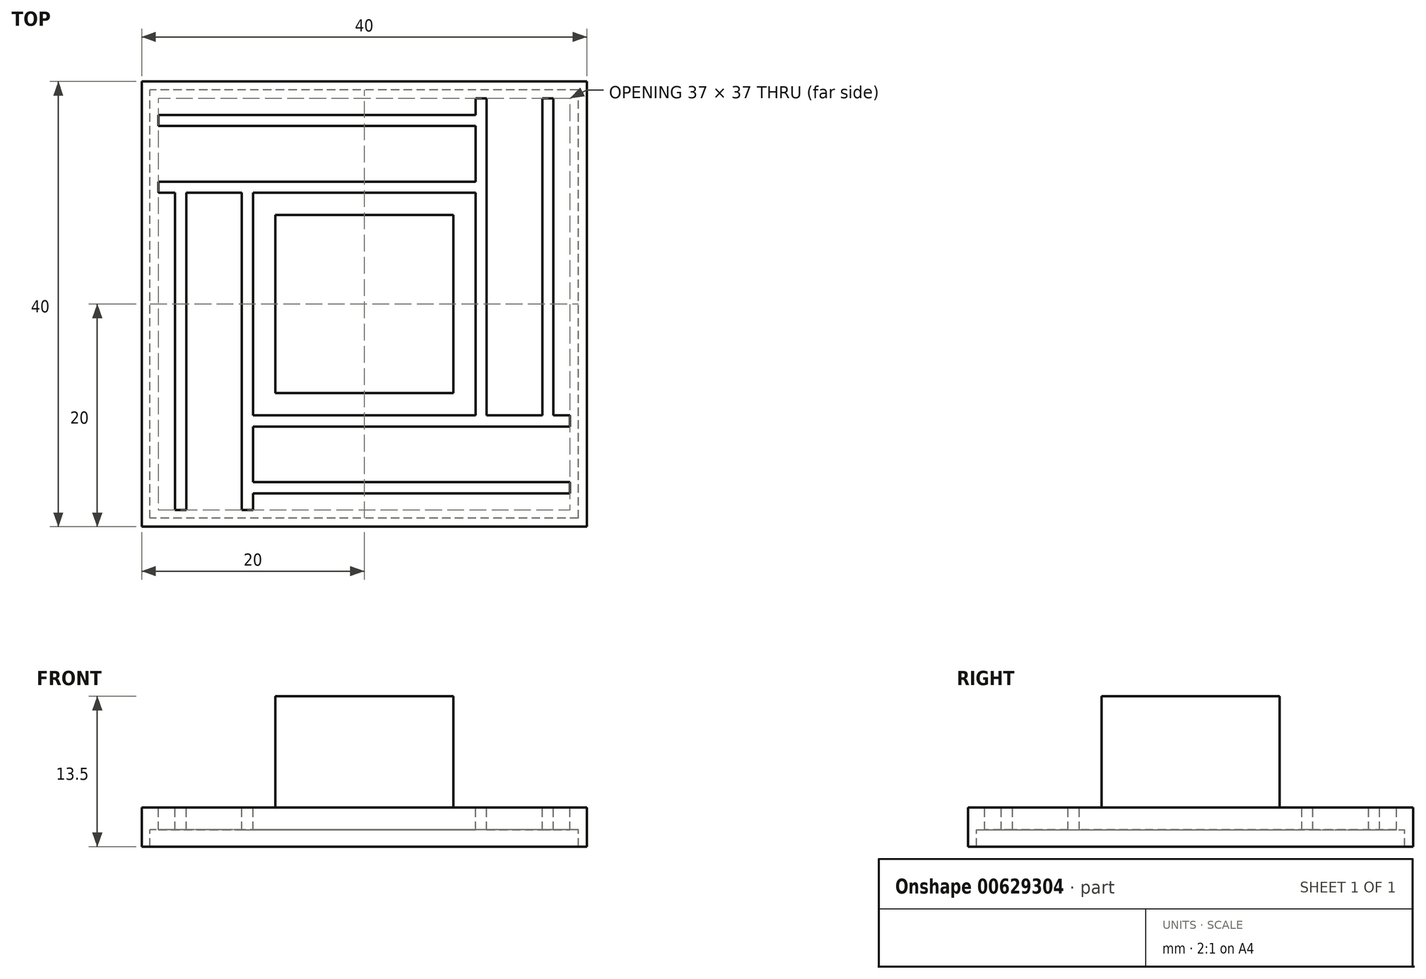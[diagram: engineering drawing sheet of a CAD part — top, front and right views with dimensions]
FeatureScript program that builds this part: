
annotation { "Feature Type Name" : "Feature", "Feature Type Description" : "" }
export const myFeature = defineFeature(function(context is Context, id is Id, definition is map)
    precondition{}
    {
        {
            var Q0;
            Q0=qCreatedBy(makeId("Top.planeOp"),FACE);
            var sketch = newSketch(context, id + "F0", { "sketchPlane" : qUnion([Q0])});
            skLineSegment(sketch, "E0.bottom", {"start": v(20, 20) * mm, "end": v(-20, 20) * mm});
            skLineSegment(sketch, "E0.top", {"start": v(20, -20) * mm, "end": v(-20, -20) * mm});
            skLineSegment(sketch, "E0.left", {"start": v(20, 20) * mm, "end": v(20, -20) * mm});
            skLineSegment(sketch, "E0.right", {"start": v(-20, 20) * mm, "end": v(-20, -20) * mm});
            skPoint(sketch, "E0.middle", {"position": v(0, 0) * mm});
            skSolve(sketch);
        }
        {
            var Q0;
            Q0 = qSketchRegion(id + "F0", true);
            extrude(context, id + "F1", {"entities" : qUnion([Q0]), "depth" : 2 * mm, "offsetDistance" : 25 * mm});
        }
        {
            var Q0;
            Q0=makeQuery(id+"F1.opExtrude","CAP_FACE",FACE,{"disambiguationData":[OSD([sQuery(id+"F0.wireOp",EDGE,"E0.bottom"),sQuery(id+"F0.wireOp",EDGE,"E0.top"),sQuery(id+"F0.wireOp",EDGE,"E0.left"),sQuery(id+"F0.wireOp",EDGE,"E0.right")])],"isStart":true});
            var sketch = newSketch(context, id + "F2", { "sketchPlane" : qUnion([Q0])});
            skLineSegment(sketch, "E1.bottom", {"start": v(19.25, 19.25) * mm, "end": v(-19.25, 19.25) * mm});
            skLineSegment(sketch, "E1.top", {"start": v(19.25, -19.25) * mm, "end": v(-19.25, -19.25) * mm});
            skLineSegment(sketch, "E1.left", {"start": v(19.25, 19.25) * mm, "end": v(19.25, -19.25) * mm});
            skLineSegment(sketch, "E1.right", {"start": v(-19.25, 19.25) * mm, "end": v(-19.25, -19.25) * mm});
            skPoint(sketch, "E1.middle", {"position": v(0, 0) * mm});
            skSolve(sketch);
        }
        {
            var Q0;
            Q0=makeQuery(id+"F2.imprint","IMPRINT",FACE,{"disambiguationData":[TD([[makeQuery(id+"F2.imprint","IMPRINT",EDGE,{"derivedFrom":sQuery(id+"F2.wireOp",EDGE,"E1.bottom")}),-1.0]])]});
            extrude(context, id + "F3", {"entities" : qUnion([Q0]), "operationType" : NewBodyOperationType.ADD, "depth" : 1.5 * mm, "offsetDistance" : 25 * mm});
        }
        {
            var Q0;
            Q0=makeQuery(id+"F1.opExtrude","CAP_FACE",FACE,{"disambiguationData":[OSD([sQuery(id+"F0.wireOp",EDGE,"E0.bottom"),sQuery(id+"F0.wireOp",EDGE,"E0.top"),sQuery(id+"F0.wireOp",EDGE,"E0.left"),sQuery(id+"F0.wireOp",EDGE,"E0.right")])],"isStart":false});
            var sketch = newSketch(context, id + "F4", { "sketchPlane" : qUnion([Q0])});
            skLineSegment(sketch, "E2.bottom", {"start": v(10, 10) * mm, "end": v(-10, 10) * mm});
            skLineSegment(sketch, "E2.top", {"start": v(10, -10) * mm, "end": v(-10, -10) * mm});
            skLineSegment(sketch, "E2.left", {"start": v(10, 10) * mm, "end": v(10, -10) * mm});
            skLineSegment(sketch, "E2.right", {"start": v(-10, 10) * mm, "end": v(-10, -10) * mm});
            skPoint(sketch, "E2.middle", {"position": v(0, 0) * mm});
            skSolve(sketch);
        }
        {
            var Q0;
            Q0=makeQuery(id+"F1.opExtrude","CAP_FACE",FACE,{"disambiguationData":[OSD([sQuery(id+"F0.wireOp",EDGE,"E0.bottom"),sQuery(id+"F0.wireOp",EDGE,"E0.top"),sQuery(id+"F0.wireOp",EDGE,"E0.left"),sQuery(id+"F0.wireOp",EDGE,"E0.right")])],"isStart":false});
            var sketch = newSketch(context, id + "F5", { "sketchPlane" : qUnion([Q0])});
            skLineSegment(sketch, "E3.bottom", {"start": v(10, 10) * mm, "end": v(-10, 10) * mm, "construction": true});
            skLineSegment(sketch, "E3.top", {"start": v(10, -10) * mm, "end": v(-10, -10) * mm, "construction": true});
            skLineSegment(sketch, "E3.left", {"start": v(10, 10) * mm, "end": v(10, -10) * mm, "construction": true});
            skLineSegment(sketch, "E3.right", {"start": v(-10, 10) * mm, "end": v(-10, -10) * mm, "construction": true});
            skPoint(sketch, "E3.middle", {"position": v(0, 0) * mm});
            skLineSegment(sketch, "E4", {"start": v(-10, -10) * mm, "end": v(-10, -16) * mm, "construction": true});
            skLineSegment(sketch, "E5", {"start": v(-10, -16) * mm, "end": v(17.5, -16) * mm, "construction": true});
            skLineSegment(sketch, "E6", {"start": v(-5, -10) * mm, "end": v(-5, -11) * mm, "construction": true});
            skLineSegment(sketch, "E7", {"start": v(-5, -11) * mm, "end": v(17.5, -11) * mm, "construction": true});
            skLineSegment(sketch, "E8", {"start": v(17.5, -11) * mm, "end": v(17.5, -16) * mm, "construction": true});
            skLineSegment(sketch, "E9.0", {"start": v(18.5, -11) * mm, "end": v(18.5, -17) * mm, "construction": true});
            skLineSegment(sketch, "E9.1", {"start": v(-11, -17) * mm, "end": v(18.5, -17) * mm, "construction": true});
            skLineSegment(sketch, "E9.2", {"start": v(-11, -10) * mm, "end": v(-11, -17) * mm, "construction": true});
            skLineSegment(sketch, "E10", {"start": v(-5, -10) * mm, "end": v(-5, -11) * mm});
            skLineSegment(sketch, "E11", {"start": v(-5, -11) * mm, "end": v(18.5, -11) * mm});
            skLineSegment(sketch, "E12", {"start": v(-5, -10) * mm, "end": v(18.5, -10) * mm});
            skLineSegment(sketch, "E13", {"start": v(18.5, -11) * mm, "end": v(18.5, -10) * mm});
            skLineSegment(sketch, "E14", {"start": v(-10, -10) * mm, "end": v(-10, -16) * mm});
            skLineSegment(sketch, "E15", {"start": v(-10, -16) * mm, "end": v(18.5, -16) * mm});
            skLineSegment(sketch, "E16", {"start": v(18.5, -16) * mm, "end": v(18.5, -17) * mm});
            skLineSegment(sketch, "E17", {"start": v(18.5, -17) * mm, "end": v(-11, -17) * mm});
            skLineSegment(sketch, "E18.bottom", {"start": v(11, 11) * mm, "end": v(-11, 11) * mm, "construction": true});
            skLineSegment(sketch, "E18.top", {"start": v(11, -11) * mm, "end": v(-11, -11) * mm, "construction": true});
            skLineSegment(sketch, "E18.left", {"start": v(11, 11) * mm, "end": v(11, -11) * mm, "construction": true});
            skLineSegment(sketch, "E18.right", {"start": v(-11, 11) * mm, "end": v(-11, -11) * mm, "construction": true});
            skLineSegment(sketch, "E19", {"start": v(-10, -16) * mm, "end": v(-10, 11) * mm});
            skLineSegment(sketch, "E20", {"start": v(-10, 11) * mm, "end": v(-11, 11) * mm});
            skLineSegment(sketch, "E21", {"start": v(-11, 11) * mm, "end": v(-11, -17) * mm});
            skLineSegment(sketch, "E22.1.0", {"start": v(17, -11) * mm, "end": v(17, 18.5) * mm, "construction": true});
            skLineSegment(sketch, "E22.1.1", {"start": v(11, 17.5) * mm, "end": v(16, 17.5) * mm, "construction": true});
            skLineSegment(sketch, "E22.1.2", {"start": v(11, -5) * mm, "end": v(11, 17.5) * mm, "construction": true});
            skLineSegment(sketch, "E22.1.4", {"start": v(16, -10) * mm, "end": v(16, 17.5) * mm, "construction": true});
            skLineSegment(sketch, "E22.1.5", {"start": v(11, 18.5) * mm, "end": v(17, 18.5) * mm, "construction": true});
            skLineSegment(sketch, "E22.1.7", {"start": v(10, -5) * mm, "end": v(10, 18.5) * mm});
            skLineSegment(sketch, "E22.1.9", {"start": v(10, -10) * mm, "end": v(16, -10) * mm, "construction": true});
            skLineSegment(sketch, "E22.1.10", {"start": v(10, -11) * mm, "end": v(17, -11) * mm, "construction": true});
            skLineSegment(sketch, "E22.1.11", {"start": v(16, -10) * mm, "end": v(16, 18.5) * mm});
            skLineSegment(sketch, "E22.1.12", {"start": v(11, -5) * mm, "end": v(11, 18.5) * mm});
            skLineSegment(sketch, "E22.1.13", {"start": v(10, -10) * mm, "end": v(16, -10) * mm});
            skLineSegment(sketch, "E22.1.14", {"start": v(16, -10) * mm, "end": v(-11, -10) * mm});
            skLineSegment(sketch, "E22.1.15", {"start": v(17, 18.5) * mm, "end": v(17, -11) * mm});
            skLineSegment(sketch, "E22.1.17", {"start": v(-11, -11) * mm, "end": v(17, -11) * mm});
            skLineSegment(sketch, "E22.1.18", {"start": v(-11, -10) * mm, "end": v(-11, -11) * mm});
            skLineSegment(sketch, "E22.1.19", {"start": v(16, 18.5) * mm, "end": v(17, 18.5) * mm});
            skLineSegment(sketch, "E22.1.20", {"start": v(11, 18.5) * mm, "end": v(10, 18.5) * mm});
            skLineSegment(sketch, "E22.1.21", {"start": v(10, -5) * mm, "end": v(11, -5) * mm, "construction": true});
            skLineSegment(sketch, "E22.1.22", {"start": v(10, -5) * mm, "end": v(11, -5) * mm});
            skLineSegment(sketch, "E22.1.23", {"start": v(-10, 10) * mm, "end": v(10, 10) * mm, "construction": true});
            skLineSegment(sketch, "E22.1.26", {"start": v(-10, -10) * mm, "end": v(10, -10) * mm, "construction": true});
            skLineSegment(sketch, "E22.1.27", {"start": v(-11, -11) * mm, "end": v(11, -11) * mm, "construction": true});
            skLineSegment(sketch, "E22.1.28", {"start": v(-11, 11) * mm, "end": v(11, 11) * mm, "construction": true});
            skLineSegment(sketch, "E22.2.0", {"start": v(11, 17) * mm, "end": v(-18.5, 17) * mm, "construction": true});
            skLineSegment(sketch, "E22.2.1", {"start": v(-17.5, 11) * mm, "end": v(-17.5, 16) * mm, "construction": true});
            skLineSegment(sketch, "E22.2.2", {"start": v(5, 11) * mm, "end": v(-17.5, 11) * mm, "construction": true});
            skLineSegment(sketch, "E22.2.3", {"start": v(-11, 11) * mm, "end": v(11, 11) * mm, "construction": true});
            skLineSegment(sketch, "E22.2.4", {"start": v(10, 16) * mm, "end": v(-17.5, 16) * mm, "construction": true});
            skLineSegment(sketch, "E22.2.5", {"start": v(-18.5, 11) * mm, "end": v(-18.5, 17) * mm, "construction": true});
            skLineSegment(sketch, "E22.2.6", {"start": v(-10, 10) * mm, "end": v(10, 10) * mm, "construction": true});
            skLineSegment(sketch, "E22.2.7", {"start": v(5, 10) * mm, "end": v(-18.5, 10) * mm});
            skLineSegment(sketch, "E22.2.9", {"start": v(10, 10) * mm, "end": v(10, 16) * mm, "construction": true});
            skLineSegment(sketch, "E22.2.10", {"start": v(11, 10) * mm, "end": v(11, 17) * mm, "construction": true});
            skLineSegment(sketch, "E22.2.11", {"start": v(10, 16) * mm, "end": v(-18.5, 16) * mm});
            skLineSegment(sketch, "E22.2.12", {"start": v(5, 11) * mm, "end": v(-18.5, 11) * mm});
            skLineSegment(sketch, "E22.2.13", {"start": v(10, 10) * mm, "end": v(10, 16) * mm});
            skLineSegment(sketch, "E22.2.14", {"start": v(10, 16) * mm, "end": v(10, -11) * mm});
            skLineSegment(sketch, "E22.2.15", {"start": v(-18.5, 17) * mm, "end": v(11, 17) * mm});
            skLineSegment(sketch, "E22.2.17", {"start": v(11, -11) * mm, "end": v(11, 17) * mm});
            skLineSegment(sketch, "E22.2.18", {"start": v(10, -11) * mm, "end": v(11, -11) * mm});
            skLineSegment(sketch, "E22.2.19", {"start": v(-18.5, 16) * mm, "end": v(-18.5, 17) * mm});
            skLineSegment(sketch, "E22.2.20", {"start": v(-18.5, 11) * mm, "end": v(-18.5, 10) * mm});
            skLineSegment(sketch, "E22.2.21", {"start": v(5, 10) * mm, "end": v(5, 11) * mm, "construction": true});
            skLineSegment(sketch, "E22.2.22", {"start": v(5, 10) * mm, "end": v(5, 11) * mm});
            skLineSegment(sketch, "E22.2.23", {"start": v(-10, -10) * mm, "end": v(-10, 10) * mm, "construction": true});
            skLineSegment(sketch, "E22.2.24", {"start": v(-10, -10) * mm, "end": v(10, -10) * mm, "construction": true});
            skLineSegment(sketch, "E22.2.25", {"start": v(-11, -11) * mm, "end": v(11, -11) * mm, "construction": true});
            skLineSegment(sketch, "E22.2.26", {"start": v(10, -10) * mm, "end": v(10, 10) * mm, "construction": true});
            skLineSegment(sketch, "E22.2.27", {"start": v(11, -11) * mm, "end": v(11, 11) * mm, "construction": true});
            skLineSegment(sketch, "E22.2.28", {"start": v(-11, -11) * mm, "end": v(-11, 11) * mm, "construction": true});
            skLineSegment(sketch, "E22.3.0", {"start": v(-17, 11) * mm, "end": v(-17, -18.5) * mm, "construction": true});
            skLineSegment(sketch, "E22.3.1", {"start": v(-11, -17.5) * mm, "end": v(-16, -17.5) * mm, "construction": true});
            skLineSegment(sketch, "E22.3.2", {"start": v(-11, 5) * mm, "end": v(-11, -17.5) * mm, "construction": true});
            skLineSegment(sketch, "E22.3.3", {"start": v(-11, -11) * mm, "end": v(-11, 11) * mm, "construction": true});
            skLineSegment(sketch, "E22.3.4", {"start": v(-16, 10) * mm, "end": v(-16, -17.5) * mm, "construction": true});
            skLineSegment(sketch, "E22.3.5", {"start": v(-11, -18.5) * mm, "end": v(-17, -18.5) * mm, "construction": true});
            skLineSegment(sketch, "E22.3.6", {"start": v(-10, -10) * mm, "end": v(-10, 10) * mm, "construction": true});
            skLineSegment(sketch, "E22.3.7", {"start": v(-10, 5) * mm, "end": v(-10, -18.5) * mm});
            skLineSegment(sketch, "E22.3.9", {"start": v(-10, 10) * mm, "end": v(-16, 10) * mm, "construction": true});
            skLineSegment(sketch, "E22.3.10", {"start": v(-10, 11) * mm, "end": v(-17, 11) * mm, "construction": true});
            skLineSegment(sketch, "E22.3.11", {"start": v(-16, 10) * mm, "end": v(-16, -18.5) * mm});
            skLineSegment(sketch, "E22.3.12", {"start": v(-11, 5) * mm, "end": v(-11, -18.5) * mm});
            skLineSegment(sketch, "E22.3.13", {"start": v(-10, 10) * mm, "end": v(-16, 10) * mm});
            skLineSegment(sketch, "E22.3.14", {"start": v(-16, 10) * mm, "end": v(11, 10) * mm});
            skLineSegment(sketch, "E22.3.15", {"start": v(-17, -18.5) * mm, "end": v(-17, 11) * mm});
            skLineSegment(sketch, "E22.3.17", {"start": v(11, 11) * mm, "end": v(-17, 11) * mm});
            skLineSegment(sketch, "E22.3.18", {"start": v(11, 10) * mm, "end": v(11, 11) * mm});
            skLineSegment(sketch, "E22.3.19", {"start": v(-16, -18.5) * mm, "end": v(-17, -18.5) * mm});
            skLineSegment(sketch, "E22.3.20", {"start": v(-11, -18.5) * mm, "end": v(-10, -18.5) * mm});
            skLineSegment(sketch, "E22.3.21", {"start": v(-10, 5) * mm, "end": v(-11, 5) * mm, "construction": true});
            skLineSegment(sketch, "E22.3.22", {"start": v(-10, 5) * mm, "end": v(-11, 5) * mm});
            skLineSegment(sketch, "E22.3.24", {"start": v(10, -10) * mm, "end": v(10, 10) * mm, "construction": true});
            skLineSegment(sketch, "E22.3.25", {"start": v(11, -11) * mm, "end": v(11, 11) * mm, "construction": true});
            skSolve(sketch);
        }
        {
            var Q0;
            Q0 = qSketchRegion(id + "F5", true);
            extrude(context, id + "F6", {"entities" : qUnion([Q0]), "operationType" : NewBodyOperationType.REMOVE, "endBound" : BoundingType.THROUGH_ALL, "oppositeDirection" : true, "depth" : 25 * mm, "offsetDistance" : 25 * mm});
        }
        {
            var Q0;
            Q0=makeQuery(id+"F4.imprint","IMPRINT",FACE,{"disambiguationData":[TD([[makeQuery(id+"F4.imprint","IMPRINT",EDGE,{"derivedFrom":sQuery(id+"F4.wireOp",EDGE,"E2.bottom")}),1.0]])]});
            var sketch = newSketch(context, id + "F7", { "sketchPlane" : qUnion([Q0])});
            skLineSegment(sketch, "E23.bottom", {"start": v(8, 8) * mm, "end": v(-8, 8) * mm});
            skLineSegment(sketch, "E23.top", {"start": v(8, -8) * mm, "end": v(-8, -8) * mm});
            skLineSegment(sketch, "E23.left", {"start": v(8, 8) * mm, "end": v(8, -8) * mm});
            skLineSegment(sketch, "E23.right", {"start": v(-8, 8) * mm, "end": v(-8, -8) * mm});
            skPoint(sketch, "E23.middle", {"position": v(0, 0) * mm});
            skSolve(sketch);
        }
        {
            var Q0;
            Q0=makeQuery(id+"F7.imprint","IMPRINT",FACE,{"disambiguationData":[TD([[makeQuery(id+"F7.imprint","IMPRINT",EDGE,{"derivedFrom":sQuery(id+"F7.wireOp",EDGE,"E23.bottom")}),1.0]])]});
            extrude(context, id + "F8", {"entities" : qUnion([Q0]), "operationType" : NewBodyOperationType.ADD, "depth" : 10 * mm, "offsetDistance" : 25 * mm});
        }
    });
